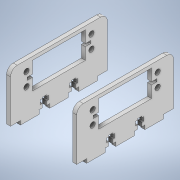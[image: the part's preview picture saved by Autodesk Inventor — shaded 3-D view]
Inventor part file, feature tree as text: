
AUTODESK INVENTOR PART (.ipt)
format: ipt  version: 2022 (Build 260153000, 153)  size: 373,760 bytes
history: native  units: mm
features: extrude x9, sketch x5, other x3, fillet x1, reference x1
ambient origin geometry x8: Origin, YZ Plane, XZ Plane, XY Plane, X Axis, Y Axis, Z Axis, Center Point
bodies: Solid1 (feature_tree)
feature tree (19):
  extrude  "Extrusion1"  Depth=37.3mm
  extrude  "Extrusion2"  Depth=3.0mm TaperAngle=0.0deg
  fillet  "Fillet1"  Radius=5.0mm
  extrude  "Extrusion4"  Depth=16.5mm
  extrude  "Extrusion5"  Depth=46.9mm
  extrude  "Extrusion6"  Depth=3.0mm TaperAngle=0.0deg
  extrude  "Extrusion7"  Depth=3.0mm TaperAngle=0.0deg
  extrude  "Extrusion8"  Depth=3.0mm TaperAngle=0.0deg
  extrude  "Extrusion9"  TaperAngle=0.0deg  [1 undecoded]
  extrude  "Extrusion10"  Depth=10.0mm TaperAngle=0.0deg
  reference  "Reference1"
  sketch  "Sketch4"  dims[d0=3.0mm d1=37.3mm]
  sketch  "Sketch6"  dims[d3=73.0mm d4=0.0mm]
  sketch  "Sketch7"  dims[d5=35.0mm d6=14.8mm d7=40.0mm d8=20.0mm d9=14.8mm d10=3.0mm d11=8.05mm d12=0.0mm d13=0.0mm d14=5.0mm]
  sketch  "Sketch9"  dims[d19=38.0mm d20=16.5mm]
  sketch  "Sketch10"  dims[d22=3.0mm d23=46.9mm d24=3.0mm d25=0.0mm d34=3.0mm d35=0.0mm d43=3.0mm d44=0.0mm d64=0.0mm d65=0.0mm d66=10.0mm d67=0.0mm d68=3.0mm d69=0.0mm d70=3.0mm d71=0.0mm d78=3.0mm d79=14.0mm d80=8.0mm d81=14.0mm d82=8.0mm d83=14.0mm d84=7.5mm d85=7.5mm d89=3.0mm d92=3.1mm d96=1.5mm d98=2.45mm d99=2.45mm d100=3.1mm d101=3.0mm d102=1.5mm d104=1.5mm d107=1.5mm d108=1.0mm d109=3.1mm d110=1.0mm d111=3.0mm d112=3.0mm d113=6.1mm d114=6.1mm d116=3.0mm d117=3.0mm d118=10.0mm d119=3.0mm d127=4.0mm d128=4.0mm d130=4.0mm d131=4.0mm d134=5.0mm d135=5.0mm d136=10.0mm d137=10.0mm d138=5.0mm d139=5.0mm d140=49.0mm d141=49.0mm d142=9.0mm d143=4.0mm d144=2.0mm d145=9.0mm d146=4.0mm d147=14.0mm d148=14.0mm d149=14.0mm d72=0.5mm d73=0.872665mm d74=0.5mm d75=0.872665mm]
  other  "<userpath>\rob.iam"
  other  "rob.iam"
  other  "Base4:1"
note: 1 required parameter value undecoded (feature->parameter linkage not recoverable at this tier; creation-order binding heuristic only, values carry confidence <= 0.55)
